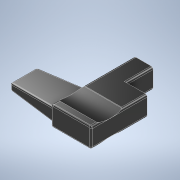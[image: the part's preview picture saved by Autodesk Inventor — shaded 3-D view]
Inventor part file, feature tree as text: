
AUTODESK INVENTOR PART (.ipt)
format: ipt  version: 2021 (Build 250183000, 183)  size: 198,656 bytes
history: native  units: mm
features: extrude x4, sketch x4, fillet x3, projected_geometry x2
ambient origin geometry x8: Origin, YZ Plane, XZ Plane, XY Plane, X Axis, Y Axis, Z Axis, Center Point
bodies: Solid1 (feature_tree)
feature tree (13):
  extrude  "Extrusion1"  Depth=14.64mm
  extrude  "Extrusion3"  Depth=7.0mm
  fillet  "Fillet1"  Radius=7.25mm
  extrude  "Extrusion4"  Depth=30.0mm
  fillet  "Fillet2"  Radius=4.65mm
  extrude  "Extrusion5"  Depth=0.5mm
  fillet  "Fillet3"  [1 undecoded]
  sketch  "Sketch1"  dims[d1=27.8mm d2=14.64mm]
  sketch  "Sketch3"  dims[d3=18.0mm d4=7.0mm d5=7.25mm d6=0.0mm]
  sketch  "Sketch4"  dims[d11=30.0mm d12=30.0mm d13=4.65mm]
  projected_geometry  "Projected Loop1"
  sketch  "Sketch5"  dims[d14=5.8mm d15=17.9mm d16=0.0mm d17=0.0mm d18=0.75mm d19=2.5mm d20=0.0mm d21=0.5mm d22=12.0mm d23=4.8mm d24=16.5mm d25=-0.698132mm d26=0.5mm]
  projected_geometry  "Projected Loop2"
note: 1 required parameter value undecoded (feature->parameter linkage not recoverable at this tier; creation-order binding heuristic only, values carry confidence <= 0.55)
